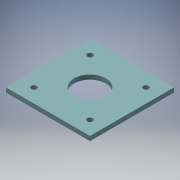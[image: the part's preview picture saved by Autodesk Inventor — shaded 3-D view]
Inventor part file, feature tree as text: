
AUTODESK INVENTOR PART (.ipt)
format: ipt  version: 2019 (Build 230136000, 136)  size: 134,144 bytes
history: native  units: mm
features: other x1, extrude x1, sketch x1
ambient origin geometry x8: Origin, YZ Plane, XZ Plane, XY Plane, X Axis, Y Axis, Z Axis, Center Point
bodies: Body1 (feature_tree)
feature tree (3):
  other  "Sólido1"
  extrude  "Extrusión1"  Depth=60.0mm
  sketch  "Boceto1"  dims[d0=22.6mm d1=60.0mm d2=60.0mm d3=4.0mm d4=4.0mm d5=4.0mm d6=4.0mm d8=20.0mm d9=20.0mm d10=40.0mm d11=40.0mm d12=20.0mm d13=40.0mm d14=20.0mm d15=3.18mm d16=0.0mm d17=20.0mm]
